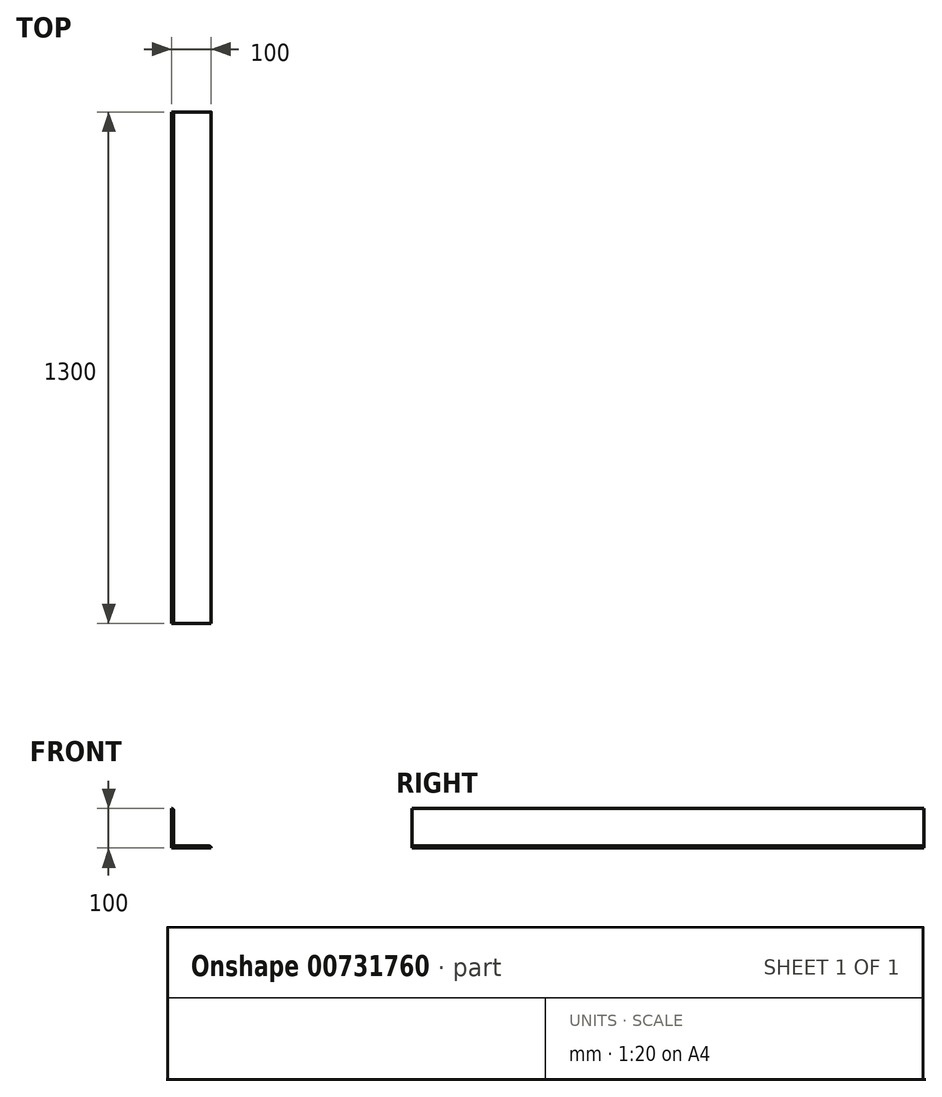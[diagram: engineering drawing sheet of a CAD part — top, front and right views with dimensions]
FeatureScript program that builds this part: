
annotation { "Feature Type Name" : "Feature", "Feature Type Description" : "" }
export const myFeature = defineFeature(function(context is Context, id is Id, definition is map)
    precondition{}
    {
        {
            var Q0;
            Q0=qCreatedBy(makeId("Front.planeOp"),FACE);
            var sketch = newSketch(context, id + "F0", { "sketchPlane" : qUnion([Q0])});
            skLineSegment(sketch, "E0.bottom", {"start": v(0, 0) * mm, "end": v(100, 0) * mm});
            skLineSegment(sketch, "E0.top", {"start": v(0, 100) * mm, "end": v(0, 100) * mm});
            skLineSegment(sketch, "E0.left", {"start": v(0, 0) * mm, "end": v(0, 100) * mm});
            skLineSegment(sketch, "E0.right", {"start": v(100, 0) * mm, "end": v(100, 0) * mm});
            skLineSegment(sketch, "E1.0", {"start": v(5, 10) * mm, "end": v(5, 95) * mm});
            skLineSegment(sketch, "E1.1", {"start": v(10, 5) * mm, "end": v(95, 5) * mm});
            skPoint(sketch, "E2.visualSharp", {"position": v(5, 100) * mm});
            skArc(sketch, "E2.filletArc", {"start": v(5, 95) * mm, "mid": v(3.54, 98.54) * mm, "end": v(0, 100) * mm});
            skPoint(sketch, "E3.visualSharp", {"position": v(5, 5) * mm});
            skArc(sketch, "E3.filletArc", {"start": v(5, 10) * mm, "mid": v(6.46, 6.46) * mm, "end": v(10, 5) * mm});
            skPoint(sketch, "E4.visualSharp", {"position": v(100, 5) * mm});
            skArc(sketch, "E4.filletArc", {"start": v(100, 0) * mm, "mid": v(98.54, 3.54) * mm, "end": v(95, 5) * mm});
            skSolve(sketch);
        }
        {
            var Q0;
            Q0 = qSketchRegion(id + "F0", true);
            extrude(context, id + "F1", {"entities" : qUnion([Q0]), "depth" : 1300 * mm, "offsetDistance" : 25 * mm});
        }
    });
